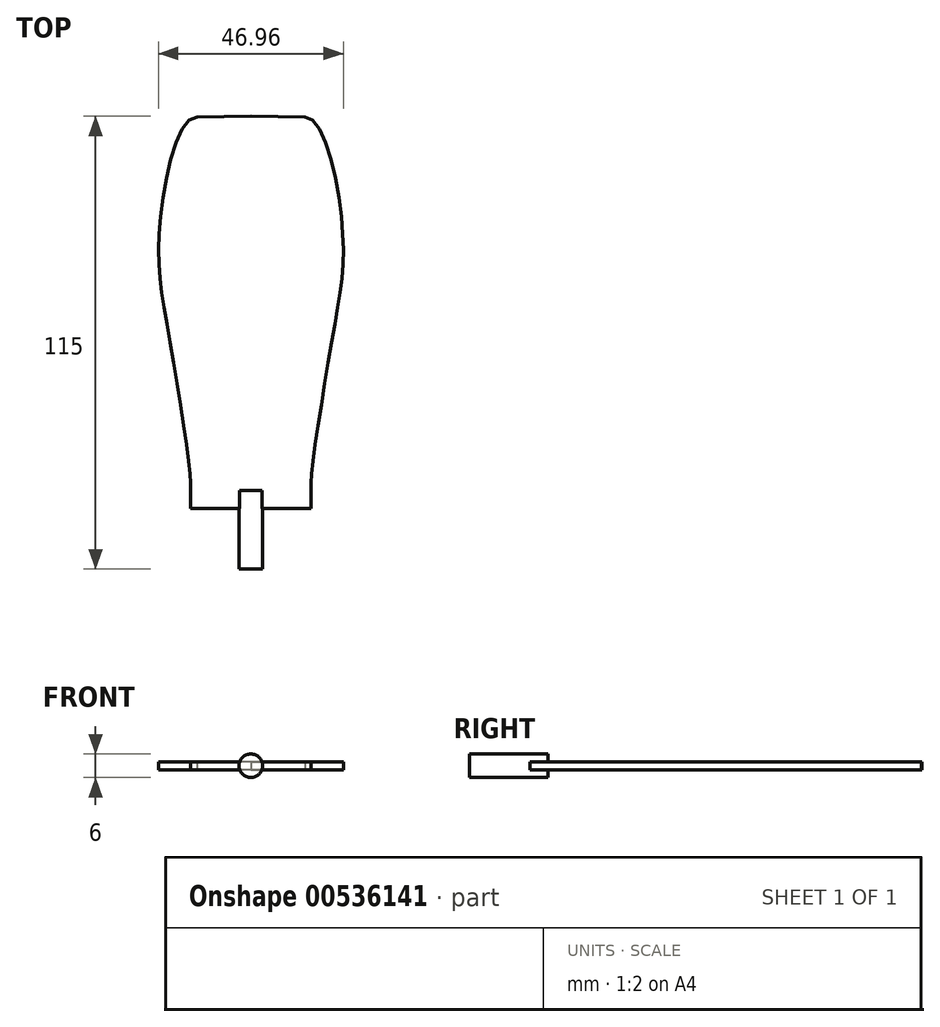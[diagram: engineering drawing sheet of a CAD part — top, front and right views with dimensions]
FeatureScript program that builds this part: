
annotation { "Feature Type Name" : "Feature", "Feature Type Description" : "" }
export const myFeature = defineFeature(function(context is Context, id is Id, definition is map)
    precondition{}
    {
        {
            var Q0;
            Q0=qCreatedBy(makeId("Top.planeOp"),FACE);
            var sketch = newSketch(context, id + "F0", { "sketchPlane" : qUnion([Q0])});
            skLineSegment(sketch, "E0", {"start": v(0, 0) * mm, "end": v(0, 115) * mm, "construction": true});
            skLineSegment(sketch, "E1", {"start": v(0, 0) * mm, "end": v(3, 0) * mm});
            skLineSegment(sketch, "E2", {"start": v(3, 0) * mm, "end": v(3, 20) * mm});
            skLineSegment(sketch, "E3", {"start": v(3, 20) * mm, "end": v(0, 20) * mm});
            skLineSegment(sketch, "E4", {"start": v(0, 20) * mm, "end": v(0, 0) * mm});
            skLineSegment(sketch, "E5", {"start": v(0, 15.4) * mm, "end": v(15.3, 15.4) * mm});
            skLineSegment(sketch, "E6", {"start": v(15.3, 15.4) * mm, "end": v(15.3, 21.8) * mm});
            skFitSpline(sketch, "E7", {"points": [v(15.3, 21.8) * mm, v(20.91, 59.72) * mm, v(23.08, 88.48) * mm, v(13.7, 114.87) * mm], "startDerivative": vector(0.15, 39.67) * mm, "endDerivative": vector(-47.55, -0.04) * mm});
            skLineSegment(sketch, "E8", {"start": v(0, 115) * mm, "end": v(13.7, 114.87) * mm});
            skLineSegment(sketch, "E9.MirrorCS", {"start": v(0, 15.4) * mm, "end": v(-15.3, 15.4) * mm});
            skLineSegment(sketch, "E10.MirrorCS", {"start": v(-15.3, 15.4) * mm, "end": v(-15.3, 21.8) * mm});
            skFitSpline(sketch, "E11.MirrorCS", {"points": [v(-15.3, 21.8) * mm, v(-20.91, 59.72) * mm, v(-23.08, 88.48) * mm, v(-13.7, 114.87) * mm], "startDerivative": vector(-0.15, 39.67) * mm, "endDerivative": vector(47.55, -0.04) * mm});
            skLineSegment(sketch, "E12.MirrorCS", {"start": v(0, 115) * mm, "end": v(-13.7, 114.87) * mm});
            skSolve(sketch);
        }
        {
            var Q0;
            {var subQ0=sQuery(id+"F0.wireOp",EDGE,"E3");Q0=makeQuery(id+"F0.imprint","IMPRINT",FACE,{"disambiguationData":[TD([[makeQuery(id+"F0.imprint","IMPRINT",EDGE,{"derivedFrom":subQ0}),1.0]])]});}
            var Q1;
            {var subQ0=sQuery(id+"F0.wireOp",EDGE,"E1");Q1=makeQuery(id+"F0.imprint","IMPRINT",FACE,{"disambiguationData":[TD([[makeQuery(id+"F0.imprint","IMPRINT",EDGE,{"derivedFrom":subQ0}),1.0]])]});}
            var Q2;
            Q2=sQuery(id+"F0.wireOp",EDGE,"E4");
            revolve(context, id + "F1", {"entities" : qUnion([Q0, Q1]), "axis" : qUnion([Q2]), "revolveType" : RevolveType.FULL});
        }
        {
            var Q0;
            {var subQ2=sQuery(id+"F0.wireOp",EDGE,"E3");Q0=makeQuery(id+"F0.imprint","IMPRINT",FACE,{"disambiguationData":[TD([[makeQuery(id+"F0.imprint","IMPRINT",EDGE,{"derivedFrom":subQ2}),-1.0]])]});}
            var Q1;
            {var subQ0=sQuery(id+"F0.wireOp",EDGE,"E3");Q1=makeQuery(id+"F0.imprint","IMPRINT",FACE,{"disambiguationData":[TD([[makeQuery(id+"F0.imprint","IMPRINT",EDGE,{"derivedFrom":subQ0}),1.0]])]});}
            extrude(context, id + "F2", {"entities" : qUnion([Q0, Q1]), "operationType" : NewBodyOperationType.ADD, "depth" : 2 * mm, "symmetric" : true});
        }
    });
